# Revit family: Drain_Roof_15_Inch_Round_Deep_Sump_Zurn-Z104
name_source: partatom
category: Plumbing Fixtures
units: mm (PartAtom-declared; Revit-internal decimal feet)

## family parameters
Always vertical = Yes
Cut with Voids When Loaded = No
Maintain Annotation Orientation = No
OmniClass Number = 23.70.50.21.24.11
OmniClass Title = Roof Waste Water Drains
Part Type = Normal
Room Calculation Point = No
Round Connector Dimension = Use Radius
Shared = No
Work Plane-Based = No

## types (18) — shared parameters
Approx. Weight (Lbs) = 46 "
Assembly Code = D2040200
CW Connection = No
Default Elevation = 20 "
Description = 15 INCH DIAMETER SUMP ROOF DRAIN W/ LOW SILHOUETTE DOME
Dome Open Area (Sq. In.) = 103 in²
HW Connection = No
Main Material = Iron - Zurn - Cast - Painted - Blue
Manufacturer = Zurn Water, LLC
Manufacurer Brand = Zurn
Modified Date = 01/09/2026
Product Documentation Link = https://files.zurn.com
Product Page URL = https://www.zurn.com
Product data url = https://www.bimobject.com
URL = www.zurn.com
Vent Connection = No
WFU = 1
Waste Connection = Yes
zero-valued in all types: CWFU, HWFU

## per-type parameters (varying)
| type | Body HT Dim 'E' | Dome Material | Model | Pipe Size 'A' (Inner Diameter) | Pipe Size 'A' (Inner Radius) | Pipe Size 'A' (Nominal Diameter) | Pipe Size 'A' (Nominal Radius) | Pipe Size 'A' (Outer Diameter) | Pipe Size 'A' (Outer Radius) | Type Comments |
| Z104-3NH | 10 " | Polypropylene - Zurn - Black | Z104 | 3.068 " | 1.534 " | 3 " | 1.5 " | 3.5 " | 1.75 " | Z104 - 3 Inch No-Hub Outlet |
| Z104-4NH | 10 " | Polypropylene - Zurn - Black | Z104 | 4.026 " | 2.013 " | 4 " | 2 " | 4.5 " | 2.25 " | Z104 - 4 Inch No-Hub Outlet |
| Z104-6NH | 10 " | Polypropylene - Zurn - Black | Z104 | 6.065 " | 3.033 " | 6 " | 3 " | 6.625 " | 3.313 " | Z104 - 6 Inch No-Hub Outlet |
| Z104-8NH | 10 " | Polypropylene - Zurn - Black | Z104 | 7.981 " | 3.991 " | 8 " | 4 " | 8.625 " | 4.313 " | Z104 - 8 Inch No-Hub Outlet |
| ZA104-3NH | 10 " | Aluminum - Zurn - Cast | ZA104 | 3.068 " | 1.534 " | 3 " | 1.5 " | 3.5 " | 1.75 " | ZA104 - 3 Inch No-Hub Outlet |
| ZA104-4NH | 10 " | Aluminum - Zurn - Cast | ZA104 | 4.026 " | 2.013 " | 4 " | 2 " | 4.5 " | 2.25 " | ZA104 - 4 Inch No-Hub Outlet |
| ZA104-6NH | 10 " | Aluminum - Zurn - Cast | ZA104 | 6.065 " | 3.033 " | 6 " | 3 " | 6.625 " | 3.313 " | ZA104 - 6 Inch No-Hub Outlet |
| ZA104-8NH | 10 " | Aluminum - Zurn - Cast | ZA104 | 7.981 " | 3.991 " | 8 " | 4 " | 8.625 " | 4.313 " | ZA104 - 8 Inch No-Hub Outlet |
| ZC104-3NH | 10 " | Iron - Zurn - Cast - Painted - Blue | ZC104 | 3.068 " | 1.534 " | 3 " | 1.5 " | 3.5 " | 1.75 " | ZC104 - 3 Inch No-Hub Outlet |
| ZC104-4NH | 10 " | Iron - Zurn - Cast - Painted - Blue | ZC104 | 4.026 " | 2.013 " | 4 " | 2 " | 4.5 " | 2.25 " | ZC104 - 4 Inch No-Hub Outlet |
| ZC104-6NH | 10 " | Iron - Zurn - Cast - Painted - Blue | ZC104 | 6.065 " | 3.033 " | 6 " | 3 " | 6.625 " | 3.313 " | ZC104 - 6 Inch No-Hub Outlet |
| ZC104-8NH | 10 " | Iron - Zurn - Cast - Painted - Blue | ZC104 | 7.981 " | 3.991 " | 8 " | 4 " | 8.625 " | 4.313 " | ZC104 - 8 Inch No-Hub Outlet |
| Z104-3NL | 9.313 " | Polypropylene - Zurn - Black | Z104 | 3.068 " | 1.534 " | 3 " | 1.5 " | 3.5 " | 1.75 " | Z104 - 3 Inch Neo-Loc Outlet |
| Z104-4NL | 9.313 " | Polypropylene - Zurn - Black | Z104 | 4.026 " | 2.013 " | 4 " | 2 " | 4.5 " | 2.25 " | Z104 - 4 Inch Neo-Loc Outlet |
| ZA104-3NL | 9.313 " | Aluminum - Zurn - Cast | ZA104 | 3.068 " | 1.534 " | 3 " | 1.5 " | 3.5 " | 1.75 " | ZA104 - 3 Inch Neo-Loc Outlet |
| ZA104-4NL | 9.313 " | Aluminum - Zurn - Cast | ZA104 | 4.026 " | 2.013 " | 4 " | 2 " | 4.5 " | 2.25 " | ZA104 - 4 Inch Neo-Loc Outlet |
| ZC104-3NL | 9.313 " | Iron - Zurn - Cast - Painted - Blue | ZC104 | 3.068 " | 1.534 " | 3 " | 1.5 " | 3.5 " | 1.75 " | ZC104 - 3 Inch Neo-Loc Outlet |
| ZC104-4NL | 9.313 " | Iron - Zurn - Cast - Painted - Blue | ZC104 | 4.026 " | 2.013 " | 4 " | 2 " | 4.5 " | 2.25 " | ZC104 - 4 Inch Neo-Loc Outlet |

## geometry (parser evidence)
native form markers: Blend x6, Sweep x5
no freeform markers — native parametric forms only
